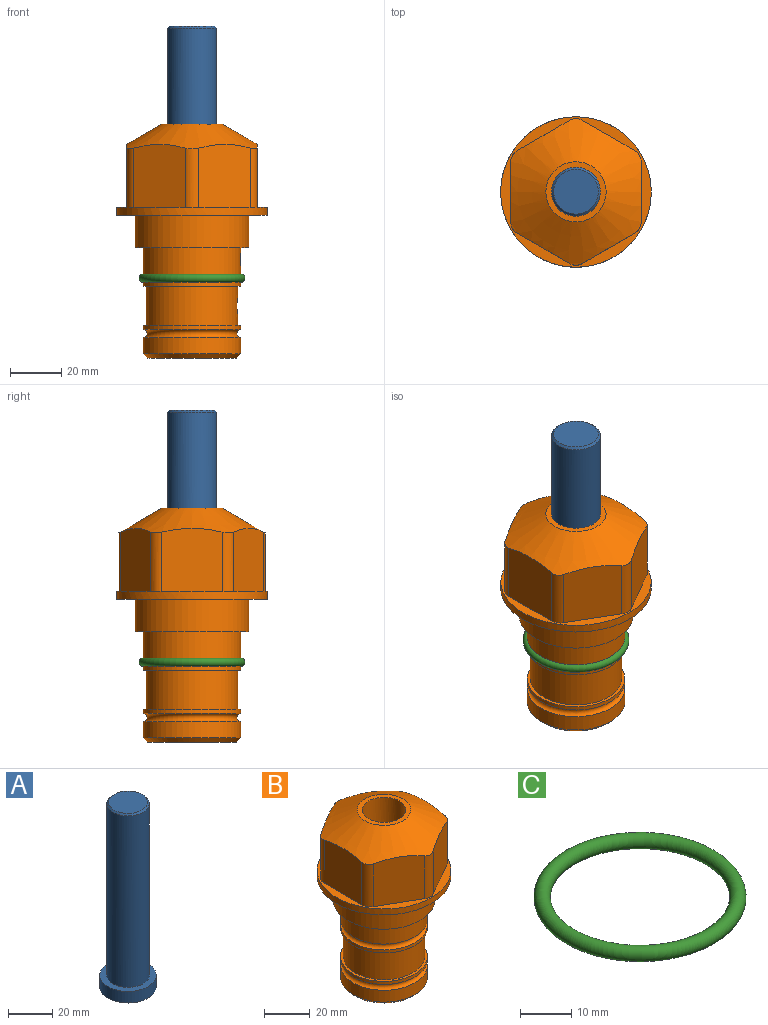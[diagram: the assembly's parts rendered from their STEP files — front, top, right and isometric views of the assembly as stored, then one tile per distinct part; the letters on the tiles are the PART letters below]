
ASSEMBLY  parts=3 mates=1
PART A: 6 faces, bbox 25.4x25.4x101.6 mm
  f0: plane 17.46x17.46mm, normal (0,0,1), area 239.5mm2, adj f5
  f1: plane 25.4x25.4mm, normal (0,0,-1), area 506.7mm2, adj f2
  f2: cylinder r=12.7mm len=25.4mm, axis (0,0,1), area 506.7mm2, adj f1,f3
  f3: plane 25.4x25.4mm, normal (0,0,1), area 221.7mm2, adj f2,f4
  f4: cylinder r=9.53mm len=94.46mm, axis (0,0,1), area 5653mm2, adj f3,f5
  f5: cone r=8.73mm half-angle=45deg, axis (0,0,-1), area 64.4mm2, adj f0,f4
PART B: 36 faces, bbox 58.7x58.7x91.2 mm
  f0: cylinder r=17.78mm len=35.56mm, axis (0,0,1), area 1670.8mm2, adj f23,f24,f31
  f1: cylinder r=19.05mm len=38.1mm, axis (0,0,1), area 1191.9mm2, adj f26,f27,f30
  f2: plane 58.66x58.66mm, normal (0,0,-1), area 1150.6mm2, adj f3,f28
  f3: cylinder r=29.33mm len=58.66mm, axis (0,0,-1), area 585.1mm2, adj f2,f4
  f4: plane 58.66x58.66mm, normal (0,0,1), area 475.9mm2, adj f3,f5,f6,f7,f8,f9,f10,f11
  f5: plane 24.5x20.32mm, normal (-0.5,0.87,0), area 562.8mm2, adj f4,f15,f16,f17
  f6: plane 24.5x20.32mm, normal (0.5,0.87,0), area 562.8mm2, adj f4,f14,f15,f17
  f7: plane 24.5x23.48mm, normal (1,0,0), area 562.8mm2, adj f4,f13,f14,f17
  f8: plane 24.5x20.32mm, normal (0.5,-0.87,0), area 562.8mm2, adj f4,f12,f13,f17
  f9: plane 24.5x20.32mm, normal (-0.5,-0.87,0), area 562.8mm2, adj f4,f11,f12,f17
  f10: plane 24.5x23.48mm, normal (-1,0,0), area 562.8mm2, adj f4,f11,f16,f17
  f11: cylinder r=5.08mm len=23.01mm, axis (0,0,-1), area 121.2mm2, adj f4,f9,f10,f17
  f12: cylinder r=5.08mm len=23.01mm, axis (0,0,-1), area 121.2mm2, adj f4,f8,f9,f17
  f13: cylinder r=5.08mm len=23.01mm, axis (0,0,-1), area 121.2mm2, adj f4,f7,f8,f17
  f14: cylinder r=5.08mm len=23.01mm, axis (0,0,-1), area 121.2mm2, adj f4,f6,f7,f17
  f15: cylinder r=5.08mm len=23.01mm, axis (0,0,-1), area 121.2mm2, adj f4,f5,f6,f17
  f16: cylinder r=5.08mm len=23.01mm, axis (0,0,-1), area 121.2mm2, adj f4,f5,f10,f17
  f17: cone r=11.73mm half-angle=60deg, axis (0,0,-1), area 2071.8mm2, adj f5,f6,f7,f8,f9,f10,f11,f12
  f18: plane 23.46x23.46mm, normal (0,0,1), area 147.4mm2, adj f17,f35
  f19: plane 34.93x34.93mm, normal (0,0,-1), area 958mm2, adj f29
  f20: cylinder r=19.05mm len=38.1mm, axis (0,0,1), area 760.1mm2, adj f21,f29
  f21: torus R=19.05mm, axis (0,0,1), area 565.3mm2, adj f20,f22
  f22: cylinder r=19.05mm len=38.1mm, axis (0,0,1), area 190mm2, adj f21,f23
  f23: plane 38.1x38.1mm, normal (0,0,1), area 146.9mm2, adj f0,f22
  f24: plane 38.1x38.1mm, normal (0,0,-1), area 146.9mm2, adj f0,f25
  f25: cylinder r=19.05mm len=38.1mm, axis (0,0,1), area 190mm2, adj f24,f26
  f26: torus R=19.05mm, axis (0,0,1), area 565.3mm2, adj f1,f25
  f27: plane 44.45x44.45mm, normal (0,0,-1), area 411.7mm2, adj f1,f28
  f28: cylinder r=22.23mm len=44.45mm, axis (0,0,1), area 1773.5mm2, adj f2,f27
  f29: cone r=19.05mm half-angle=45deg, axis (0,0,1), area 257.5mm2, adj f19,f20
  f30: cylinder r=3.17mm len=6.75mm, axis (-1,0,0), area 128mm2, adj f1,f33
  f31: cylinder r=3.17mm len=6.35mm, axis (-1,0,0), area 102.5mm2, adj f0,f33
  f32: plane 25.4x25.4mm, normal (0,0,1), area 506.7mm2, adj f33
  f33: cylinder r=12.7mm len=66.42mm, axis (0,0,-1), area 5236.2mm2, adj f30,f31,f32,f34
  f34: cone r=9.53mm half-angle=30deg, axis (0,0,-1), area 443.4mm2, adj f33,f35
  f35: cylinder r=9.53mm len=19.05mm, axis (0,0,-1), area 849mm2, adj f18,f34
PART C: 1 faces, bbox 44.7x44.7x3.2 mm
  f0: torus R=19.05mm, axis (0,0,1), area 1193.9mm2
PLACE A t=(0,0,0.14)mm
PLACE B at identity fixed
PLACE C at identity fixed
MATE slider A.f2 <-> A.f2  axis (0,0,1) through (0,0,25.78)mm
